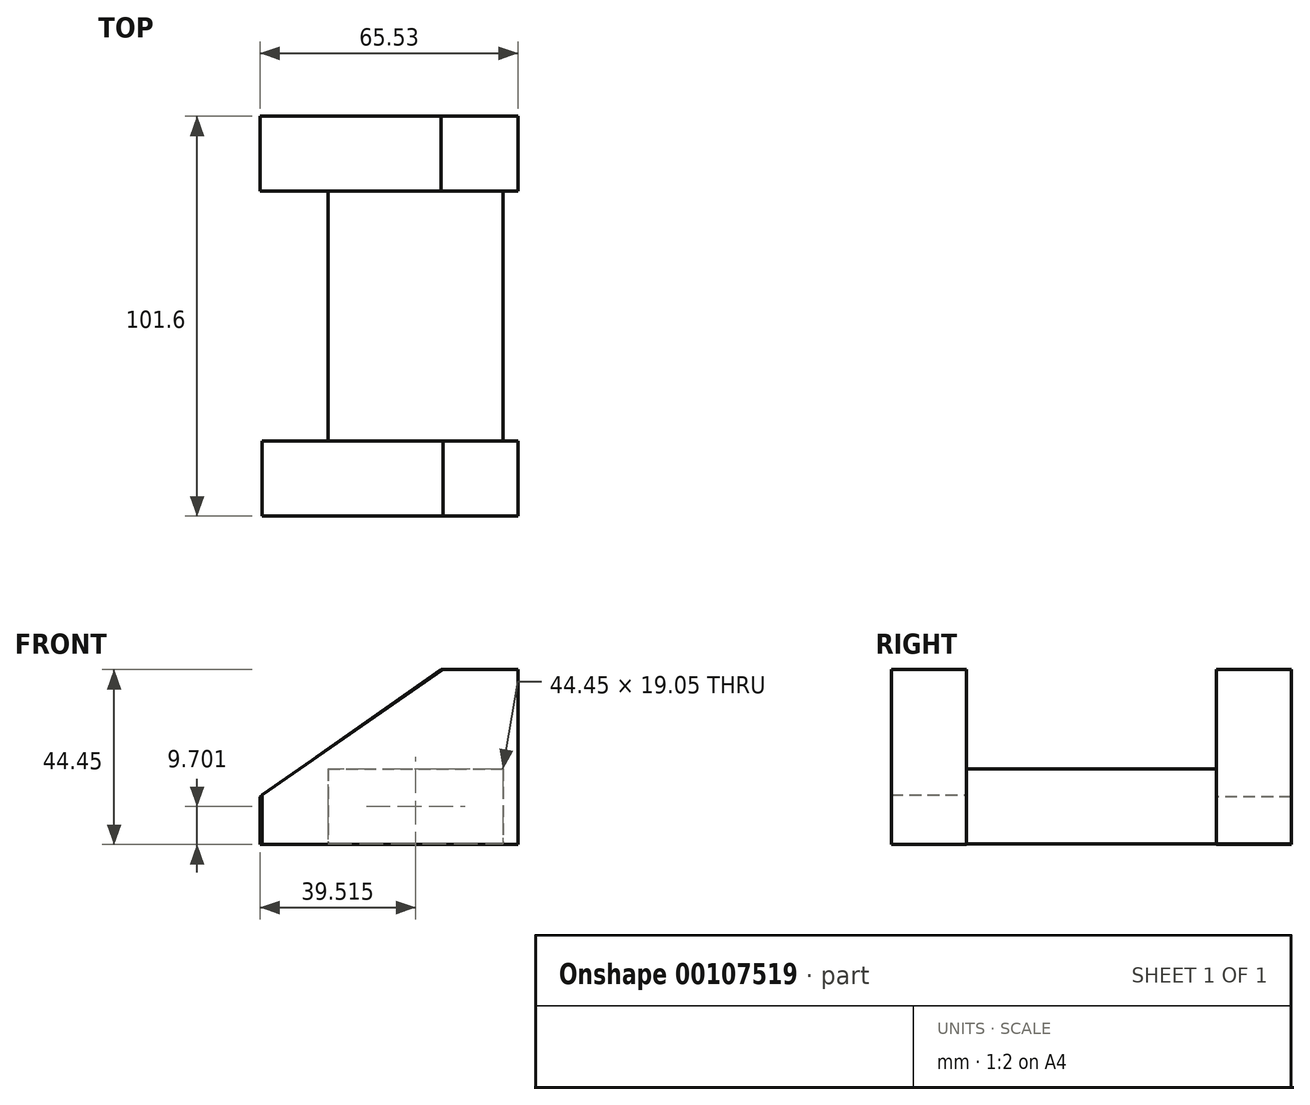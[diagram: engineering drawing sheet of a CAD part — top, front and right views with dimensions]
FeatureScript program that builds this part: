
annotation { "Feature Type Name" : "Feature", "Feature Type Description" : "" }
export const myFeature = defineFeature(function(context is Context, id is Id, definition is map)
    precondition{}
    {
        {
            var Q0;
            Q0=qCreatedBy(makeId("Front.planeOp"),FACE);
            var sketch = newSketch(context, id + "F0", { "sketchPlane" : qUnion([Q0])});
            skLineSegment(sketch, "E0", {"start": v(-61.2, -44.45) * mm, "end": v(3.8, -44.45) * mm});
            skLineSegment(sketch, "E1", {"start": v(3.8, -44.45) * mm, "end": v(3.8, 0) * mm});
            skLineSegment(sketch, "E2", {"start": v(3.8, 0) * mm, "end": v(-15.26, 0) * mm});
            skLineSegment(sketch, "E3", {"start": v(-61.2, -44.45) * mm, "end": v(-61.2, -31.76) * mm});
            skLineSegment(sketch, "E4", {"start": v(-61.2, -31.76) * mm, "end": v(-15.26, 0) * mm});
            skSolve(sketch);
        }
        {
            var Q0;
            Q0=makeQuery(id+"F0.imprint","IMPRINT",FACE,{"disambiguationData":[TD([[makeQuery(id+"F0.imprint","IMPRINT",EDGE,{"derivedFrom":sQuery(id+"F0.wireOp",EDGE,"E0")}),1.0]])]});
            extrude(context, id + "F1", {"entities" : qUnion([Q0]), "depth" : 19.05 * mm});
        }
        {
            var Q0;
            Q0=qCreatedBy(makeId("Right.planeOp"),FACE);
            var sketch = newSketch(context, id + "F2", { "sketchPlane" : qUnion([Q0])});
            skLineSegment(sketch, "E5", {"start": v(0, -44.27) * mm, "end": v(63.5, -44.27) * mm});
            skLineSegment(sketch, "E6", {"start": v(63.5, -44.27) * mm, "end": v(63.5, -25.22) * mm});
            skLineSegment(sketch, "E7", {"start": v(63.5, -25.22) * mm, "end": v(0, -25.22) * mm});
            skLineSegment(sketch, "E8", {"start": v(0, -25.22) * mm, "end": v(0, -44.27) * mm});
            skSolve(sketch);
        }
        {
            var Q0;
            Q0=makeQuery(id+"F2.imprint","IMPRINT",FACE,{"disambiguationData":[TD([[makeQuery(id+"F2.imprint","IMPRINT",EDGE,{"derivedFrom":sQuery(id+"F2.wireOp",EDGE,"E5")}),1.0]])]});
            extrude(context, id + "F3", {"entities" : qUnion([Q0]), "operationType" : NewBodyOperationType.ADD, "oppositeDirection" : true, "depth" : 44.45 * mm});
        }
        {
            var Q0;
            Q0=makeQuery(id+"F3.opExtrude","SWEPT_FACE",FACE,{"disambiguationData":[OSD([sQuery(id+"F2.wireOp",EDGE,"E6")])]});
            var sketch = newSketch(context, id + "F4", { "sketchPlane" : qUnion([Q0])});
            skLineSegment(sketch, "E9", {"start": v(0, -44.27) * mm, "end": v(-3.73, -44.27) * mm});
            skLineSegment(sketch, "E10", {"start": v(-3.73, -44.27) * mm, "end": v(-3.73, 0) * mm});
            skLineSegment(sketch, "E11", {"start": v(-3.73, 0) * mm, "end": v(15.79, 0) * mm});
            skLineSegment(sketch, "E12", {"start": v(15.79, 0) * mm, "end": v(61.74, -32.29) * mm});
            skLineSegment(sketch, "E13", {"start": v(61.74, -32.29) * mm, "end": v(61.74, -44.35) * mm});
            skLineSegment(sketch, "E14", {"start": v(61.74, -44.35) * mm, "end": v(-3.73, -44.27) * mm});
            skSolve(sketch);
        }
        {
            var Q0;
            Q0 = qSketchRegion(id + "F4", true);
            extrude(context, id + "F5", {"entities" : qUnion([Q0]), "operationType" : NewBodyOperationType.ADD, "depth" : 19.05 * mm});
        }
    });
